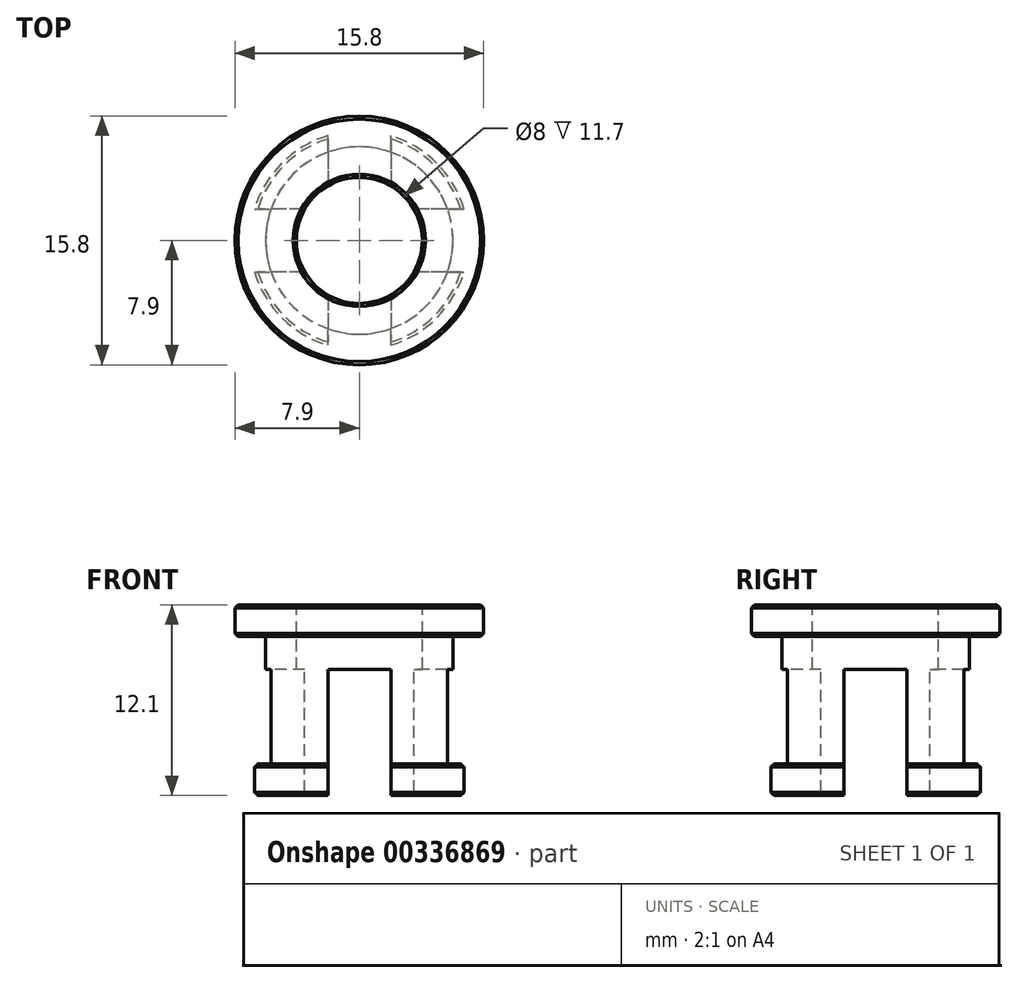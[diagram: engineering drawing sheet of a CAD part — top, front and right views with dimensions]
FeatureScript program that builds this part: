
annotation { "Feature Type Name" : "Feature", "Feature Type Description" : "" }
export const myFeature = defineFeature(function(context is Context, id is Id, definition is map)
    precondition{}
    {
        {
            var Q0;
            Q0=qCreatedBy(makeId("Front.planeOp"),FACE);
            var sketch = newSketch(context, id + "F0", { "sketchPlane" : qUnion([Q0])});
            skLineSegment(sketch, "E0", {"start": v(0, 0) * mm, "end": v(0, -12.1) * mm, "construction": true});
            skLineSegment(sketch, "E1", {"start": v(4, -12.1) * mm, "end": v(6.95, -12.1) * mm});
            skLineSegment(sketch, "E2", {"start": v(6.95, -12.1) * mm, "end": v(6.95, -10.1) * mm});
            skLineSegment(sketch, "E3", {"start": v(6.95, -10.1) * mm, "end": v(5.95, -10.1) * mm});
            skLineSegment(sketch, "E4", {"start": v(5.95, -10.1) * mm, "end": v(5.95, -2) * mm});
            skLineSegment(sketch, "E5", {"start": v(5.95, -2) * mm, "end": v(7.9, -2) * mm});
            skLineSegment(sketch, "E6", {"start": v(7.9, -2) * mm, "end": v(7.9, 0) * mm});
            skLineSegment(sketch, "E7", {"start": v(7.9, 0) * mm, "end": v(4, 0) * mm});
            skLineSegment(sketch, "E8", {"start": v(4, -12.1) * mm, "end": v(4, 0) * mm});
            skLineSegment(sketch, "E9.MirrorCS", {"start": v(-6.95, -12.1) * mm, "end": v(-6.95, -10.1) * mm, "construction": true});
            skLineSegment(sketch, "E10.MirrorCS", {"start": v(-5.95, -10.1) * mm, "end": v(-5.95, -2) * mm, "construction": true});
            skLineSegment(sketch, "E11.MirrorCS", {"start": v(-7.9, -2) * mm, "end": v(-7.9, 0) * mm, "construction": true});
            skSolve(sketch);
        }
        {
            var Q0;
            Q0=makeQuery(id+"F0.imprint","IMPRINT",FACE,{"disambiguationData":[TD([[makeQuery(id+"F0.imprint","IMPRINT",EDGE,{"derivedFrom":sQuery(id+"F0.wireOp",EDGE,"E1")}),1.0]])]});
            var Q1;
            Q1=sQuery(id+"F0.wireOp",EDGE,"E0");
            revolve(context, id + "F1", {"entities" : qUnion([Q0]), "axis" : qUnion([Q1]), "revolveType" : RevolveType.FULL});
        }
        {
            var Q0;
            Q0=makeQuery(id+"F1.opRevolve","SWEPT_FACE",FACE,{"disambiguationData":[OSD([sQuery(id+"F0.wireOp",EDGE,"E8")])]});
            var Q1;
            Q1=makeQuery(id+"F1.opRevolve","SWEPT_FACE",FACE,{"disambiguationData":[OSD([sQuery(id+"F0.wireOp",EDGE,"E6")])]});
            var Q2;
            Q2=makeQuery(id+"F1.opRevolve","SWEPT_FACE",FACE,{"disambiguationData":[OSD([sQuery(id+"F0.wireOp",EDGE,"E2")])]});
            chamfer(context, id + "F2", {"entities" : qUnion([Q0, Q1, Q2]), "width" : 0.2 * mm, "tangentPropagation" : true});
        }
        {
            var Q0;
            Q0=qCreatedBy(makeId("Front.planeOp"),FACE);
            var sketch = newSketch(context, id + "F3", { "sketchPlane" : qUnion([Q0])});
            skLineSegment(sketch, "E12.bottom", {"start": v(-2, -12.1) * mm, "end": v(2, -12.1) * mm});
            skLineSegment(sketch, "E12.top", {"start": v(-2, -4.1) * mm, "end": v(2, -4.1) * mm});
            skLineSegment(sketch, "E12.left", {"start": v(-2, -4.1) * mm, "end": v(-2, -12.1) * mm});
            skLineSegment(sketch, "E12.right", {"start": v(2, -4.1) * mm, "end": v(2, -12.1) * mm});
            skPoint(sketch, "E13", {"position": v(0, -12.1) * mm});
            skSolve(sketch);
        }
        {
            var Q0;
            Q0 = qSketchRegion(id + "F3", true);
            extrude(context, id + "F4", {"entities" : qUnion([Q0]), "operationType" : NewBodyOperationType.REMOVE, "endBound" : BoundingType.THROUGH_ALL, "oppositeDirection" : true, "depth" : 25 * mm, "hasSecondDirection" : true, "secondDirectionBound" : SecondDirectionBoundingType.THROUGH_ALL, "secondDirectionOppositeDirection" : false, "secondDirectionDepth" : 25 * mm});
        }
        {
            var Q0;
            Q0=qCreatedBy(makeId("Right.planeOp"),FACE);
            var sketch = newSketch(context, id + "F5", { "sketchPlane" : qUnion([Q0])});
            skLineSegment(sketch, "E14.bottom", {"start": v(2, -12.1) * mm, "end": v(-2, -12.1) * mm});
            skLineSegment(sketch, "E14.top", {"start": v(2, -4.1) * mm, "end": v(-2, -4.1) * mm});
            skLineSegment(sketch, "E14.left", {"start": v(2, -4.1) * mm, "end": v(2, -12.1) * mm});
            skLineSegment(sketch, "E14.right", {"start": v(-2, -4.1) * mm, "end": v(-2, -12.1) * mm});
            skPoint(sketch, "E15", {"position": v(0, -12.1) * mm});
            skSolve(sketch);
        }
        {
            var Q0;
            Q0 = qSketchRegion(id + "F5", true);
            extrude(context, id + "F6", {"entities" : qUnion([Q0]), "operationType" : NewBodyOperationType.REMOVE, "endBound" : BoundingType.THROUGH_ALL, "depth" : 25 * mm, "hasSecondDirection" : true, "secondDirectionBound" : SecondDirectionBoundingType.THROUGH_ALL, "secondDirectionOppositeDirection" : true, "secondDirectionDepth" : 25 * mm});
        }
    });
